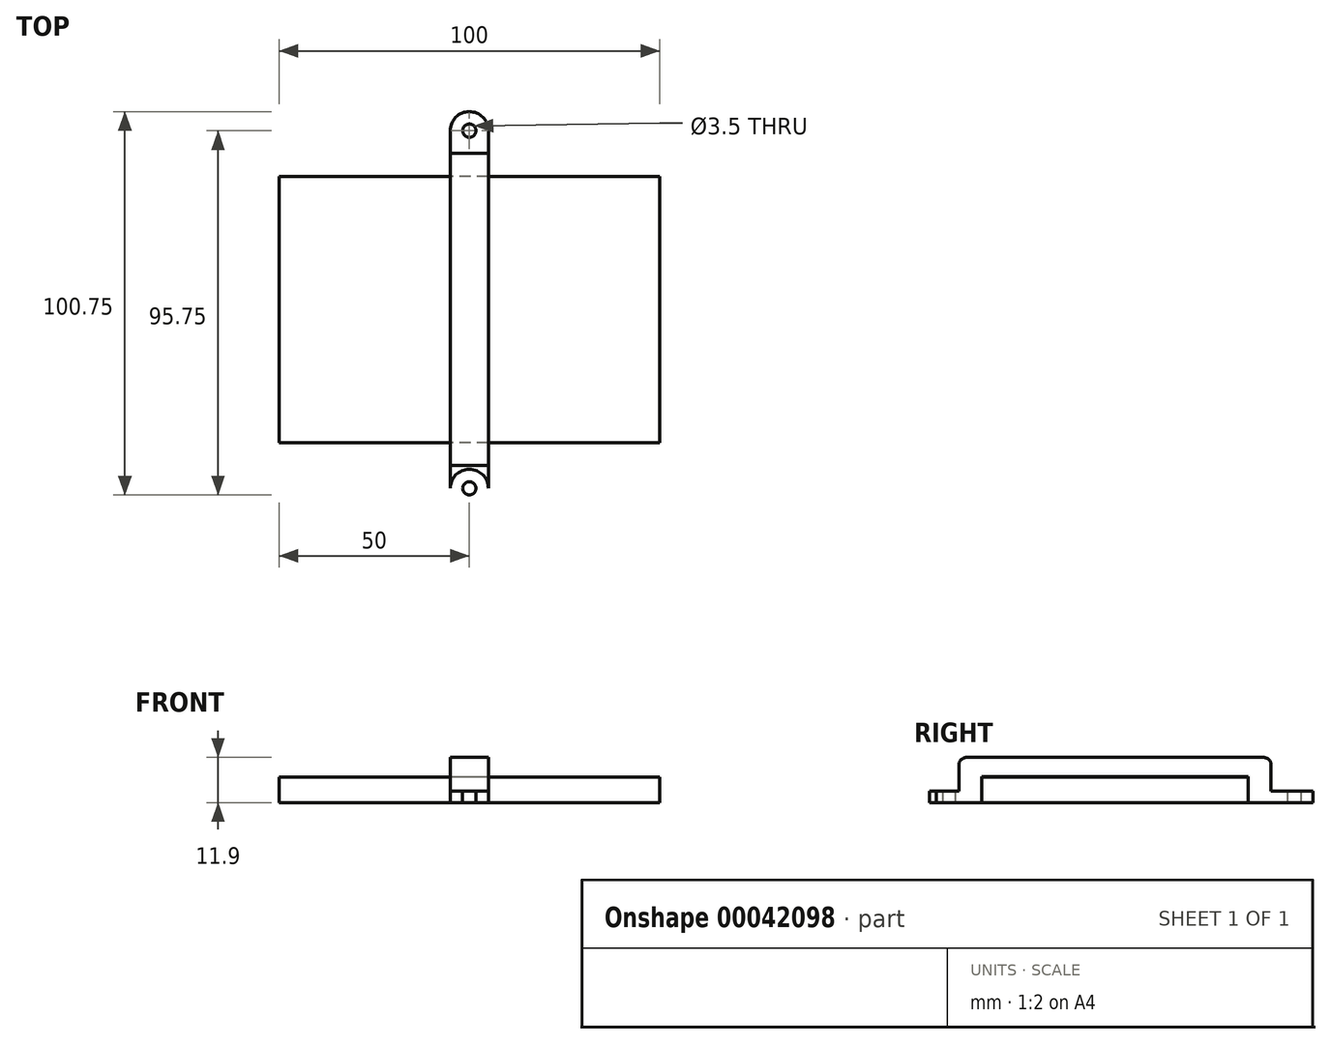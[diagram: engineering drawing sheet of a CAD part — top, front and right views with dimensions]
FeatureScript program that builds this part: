
annotation { "Feature Type Name" : "Feature", "Feature Type Description" : "" }
export const myFeature = defineFeature(function(context is Context, id is Id, definition is map)
    precondition{}
    {
        {
            var Q0;
            Q0=qCreatedBy(makeId("Top.planeOp"),FACE);
            var sketch = newSketch(context, id + "F0", { "sketchPlane" : qUnion([Q0])});
            skLineSegment(sketch, "E0.rect.bottom", {"start": v(50, -35) * mm, "end": v(-50, -35) * mm});
            skLineSegment(sketch, "E0.rect.top", {"start": v(50, 35) * mm, "end": v(-50, 35) * mm});
            skLineSegment(sketch, "E0.rect.left", {"start": v(50, -35) * mm, "end": v(50, 35) * mm});
            skLineSegment(sketch, "E0.rect.right", {"start": v(-50, -35) * mm, "end": v(-50, 35) * mm});
            skPoint(sketch, "E0.rect.middle", {"position": v(0, 0) * mm});
            skSolve(sketch);
        }
        {
            var Q0;
            Q0 = qSketchRegion(id + "F0", true);
            extrude(context, id + "F1", {"entities" : qUnion([Q0]), "depth" : 6.7 * mm});
        }
        {
            var Q0;
            Q0=qCreatedBy(makeId("Top.planeOp"),FACE);
            var sketch = newSketch(context, id + "F2", { "sketchPlane" : qUnion([Q0])});
            skCircle(sketch, "E1", {"center": v(0, 47) * mm, "radius": 1.75 * mm});
            skCircle(sketch, "E2", {"center": v(0, 47) * mm, "radius": 5 * mm});
            skLineSegment(sketch, "E3.top", {"start": v(-5, 35) * mm, "end": v(5, 35) * mm});
            skLineSegment(sketch, "E3.left", {"start": v(-5, 47) * mm, "end": v(-5, 35) * mm});
            skLineSegment(sketch, "E3.right", {"start": v(5, 47) * mm, "end": v(5, 35) * mm});
            skLineSegment(sketch, "E4", {"start": v(-5, 41) * mm, "end": v(5, 41) * mm});
            skCircle(sketch, "E5.MirrorC", {"center": v(0, -47) * mm, "radius": 5 * mm});
            skCircle(sketch, "E6.MirrorC", {"center": v(0, -47) * mm, "radius": 1.75 * mm});
            skLineSegment(sketch, "E7.MirrorCS", {"start": v(-5, -47) * mm, "end": v(-5, -35) * mm});
            skLineSegment(sketch, "E8.MirrorCS", {"start": v(-5, -41) * mm, "end": v(5, -41) * mm});
            skLineSegment(sketch, "E9.MirrorCS", {"start": v(5, -47) * mm, "end": v(5, -35) * mm});
            skLineSegment(sketch, "E10.MirrorCS", {"start": v(-5, -35) * mm, "end": v(5, -35) * mm});
            skSolve(sketch);
        }
        {
            var Q0;
            Q0=makeQuery(id+"F2.imprint","IMPRINT",FACE,{"disambiguationData":[TD([[makeQuery(id+"F2.imprint","IMPRINT",EDGE,{"derivedFrom":sQuery(id+"F2.wireOp",EDGE,"E1")}),-1.0]])]});
            var Q1;
            {var subQ1=sQuery(id+"F2.wireOp",EDGE,"E4");Q1=makeQuery(id+"F2.imprint","IMPRINT",FACE,{"disambiguationData":[TD([[makeQuery(id+"F2.imprint","IMPRINT",EDGE,{"derivedFrom":subQ1}),1.0]])]});}
            var Q2;
            Q2=makeQuery(id+"F2.imprint","IMPRINT",FACE,{"disambiguationData":[TD([[makeQuery(id+"F2.imprint","IMPRINT",EDGE,{"derivedFrom":sQuery(id+"F2.wireOp",EDGE,"E6.MirrorC")}),1.0]])]});
            var Q3;
            {var subQ3=sQuery(id+"F2.wireOp",EDGE,"E8.MirrorCS");Q3=makeQuery(id+"F2.imprint","IMPRINT",FACE,{"disambiguationData":[TD([[makeQuery(id+"F2.imprint","IMPRINT",EDGE,{"derivedFrom":subQ3}),-1.0]])]});}
            extrude(context, id + "F3", {"entities" : qUnion([Q0, Q1, Q2, Q3]), "depth" : 3 * mm});
        }
        {
            var Q0;
            {var subQ2=sQuery(id+"F2.wireOp",EDGE,"E3.top");Q0=makeQuery(id+"F2.imprint","IMPRINT",FACE,{"disambiguationData":[TD([[makeQuery(id+"F2.imprint","IMPRINT",EDGE,{"derivedFrom":subQ2}),1.0]])]});}
            var Q1;
            {var subQ2=sQuery(id+"F2.wireOp",EDGE,"E8.MirrorCS");Q1=makeQuery(id+"F2.imprint","IMPRINT",FACE,{"disambiguationData":[TD([[makeQuery(id+"F2.imprint","IMPRINT",EDGE,{"derivedFrom":subQ2}),1.0]])]});}
            extrude(context, id + "F4", {"entities" : qUnion([Q0, Q1]), "operationType" : NewBodyOperationType.ADD, "depth" : 6.9 * mm});
        }
        {
            var Q0;
            Q0=makeQuery(id+"F4.opExtrude","CAP_FACE",FACE,{"disambiguationData":[OSD([sQuery(id+"F2.wireOp",EDGE,"E3.top"),sQuery(id+"F2.wireOp",EDGE,"E3.left"),sQuery(id+"F2.wireOp",EDGE,"E3.right"),sQuery(id+"F2.wireOp",EDGE,"E4")])],"isStart":false});
            var sketch = newSketch(context, id + "F5", { "sketchPlane" : qUnion([Q0])});
            skLineSegment(sketch, "E11.bottom", {"start": v(-5, 41) * mm, "end": v(5, 41) * mm});
            skLineSegment(sketch, "E11.top", {"start": v(-5, -41) * mm, "end": v(5, -41) * mm});
            skLineSegment(sketch, "E11.left", {"start": v(-5, 41) * mm, "end": v(-5, -41) * mm});
            skLineSegment(sketch, "E11.right", {"start": v(5, 41) * mm, "end": v(5, -41) * mm});
            skSolve(sketch);
        }
        {
            var Q0;
            Q0 = qSketchRegion(id + "F5", true);
            extrude(context, id + "F6", {"entities" : qUnion([Q0]), "operationType" : NewBodyOperationType.ADD, "depth" : 5 * mm});
        }
        {
            var Q0;
            Q0=makeQuery(id+"F6.opExtrude","CAP_EDGE",EDGE,{"disambiguationData":[OSD([sQuery(id+"F5.wireOp",EDGE,"E11.bottom")])],"isStart":false});
            var Q1;
            Q1=makeQuery(id+"F6.opExtrude","CAP_EDGE",EDGE,{"disambiguationData":[OSD([sQuery(id+"F5.wireOp",EDGE,"E11.top")])],"isStart":false});
            var Q2;
            Q2=makeQuery(id+"F3.opExtrude","CAP_EDGE",EDGE,{"disambiguationData":[OSD([sQuery(id+"F2.wireOp",EDGE,"E8.MirrorCS")])],"isStart":false});
            var Q3;
            Q3=makeQuery(id+"F3.opExtrude","CAP_EDGE",EDGE,{"disambiguationData":[OSD([sQuery(id+"F2.wireOp",EDGE,"E4")])],"isStart":false});
            fillet(context, id + "F7", {"entities" : qUnion([Q0, Q1, Q2, Q3]), "radius" : 2 * mm, "tangentPropagation" : true, "allowEdgeOverflow" : false});
        }
    });
